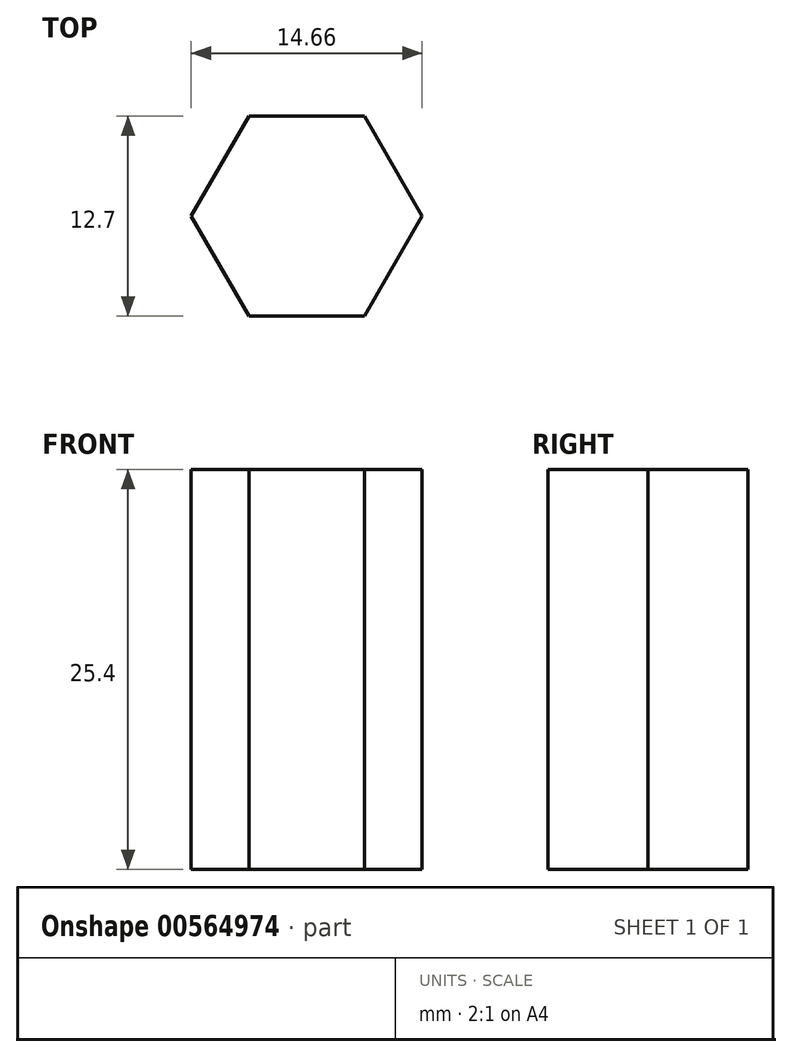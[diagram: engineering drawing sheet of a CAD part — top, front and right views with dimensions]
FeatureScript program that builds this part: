
annotation { "Feature Type Name" : "Feature", "Feature Type Description" : "" }
export const myFeature = defineFeature(function(context is Context, id is Id, definition is map)
    precondition{}
    {
        {
            var Q0;
            Q0=qCreatedBy(makeId("Top.planeOp"),FACE);
            var sketch = newSketch(context, id + "F0", { "sketchPlane" : qUnion([Q0])});
            skCircle(sketch, "E0.cCircle", {"center": v(0, 0) * mm, "radius": 6.35 * mm, "construction": true});
            skLineSegment(sketch, "E0.0", {"start": v(-3.67, 6.35) * mm, "end": v(3.67, 6.35) * mm});
            skLineSegment(sketch, "E0.1", {"start": v(3.67, 6.35) * mm, "end": v(7.33, 0) * mm});
            skLineSegment(sketch, "E0.2", {"start": v(7.33, 0) * mm, "end": v(3.67, -6.35) * mm});
            skLineSegment(sketch, "E0.3", {"start": v(3.67, -6.35) * mm, "end": v(-3.67, -6.35) * mm});
            skLineSegment(sketch, "E0.4", {"start": v(-3.67, -6.35) * mm, "end": v(-7.33, 0) * mm});
            skLineSegment(sketch, "E0.5", {"start": v(-7.33, 0) * mm, "end": v(-3.67, 6.35) * mm});
            skPoint(sketch, "E0.0.midPoint", {"position": v(0, 6.35) * mm});
            skSolve(sketch);
        }
        {
            var Q0;
            Q0=makeQuery(id+"F0.imprint","IMPRINT",FACE,{"disambiguationData":[TD([[makeQuery(id+"F0.imprint","IMPRINT",EDGE,{"derivedFrom":sQuery(id+"F0.wireOp",EDGE,"E0.0")}),-1.0]])]});
            extrude(context, id + "F1", {"entities" : qUnion([Q0]), "depth" : 25.4 * mm, "offsetDistance" : 25.4 * mm});
        }
    });
